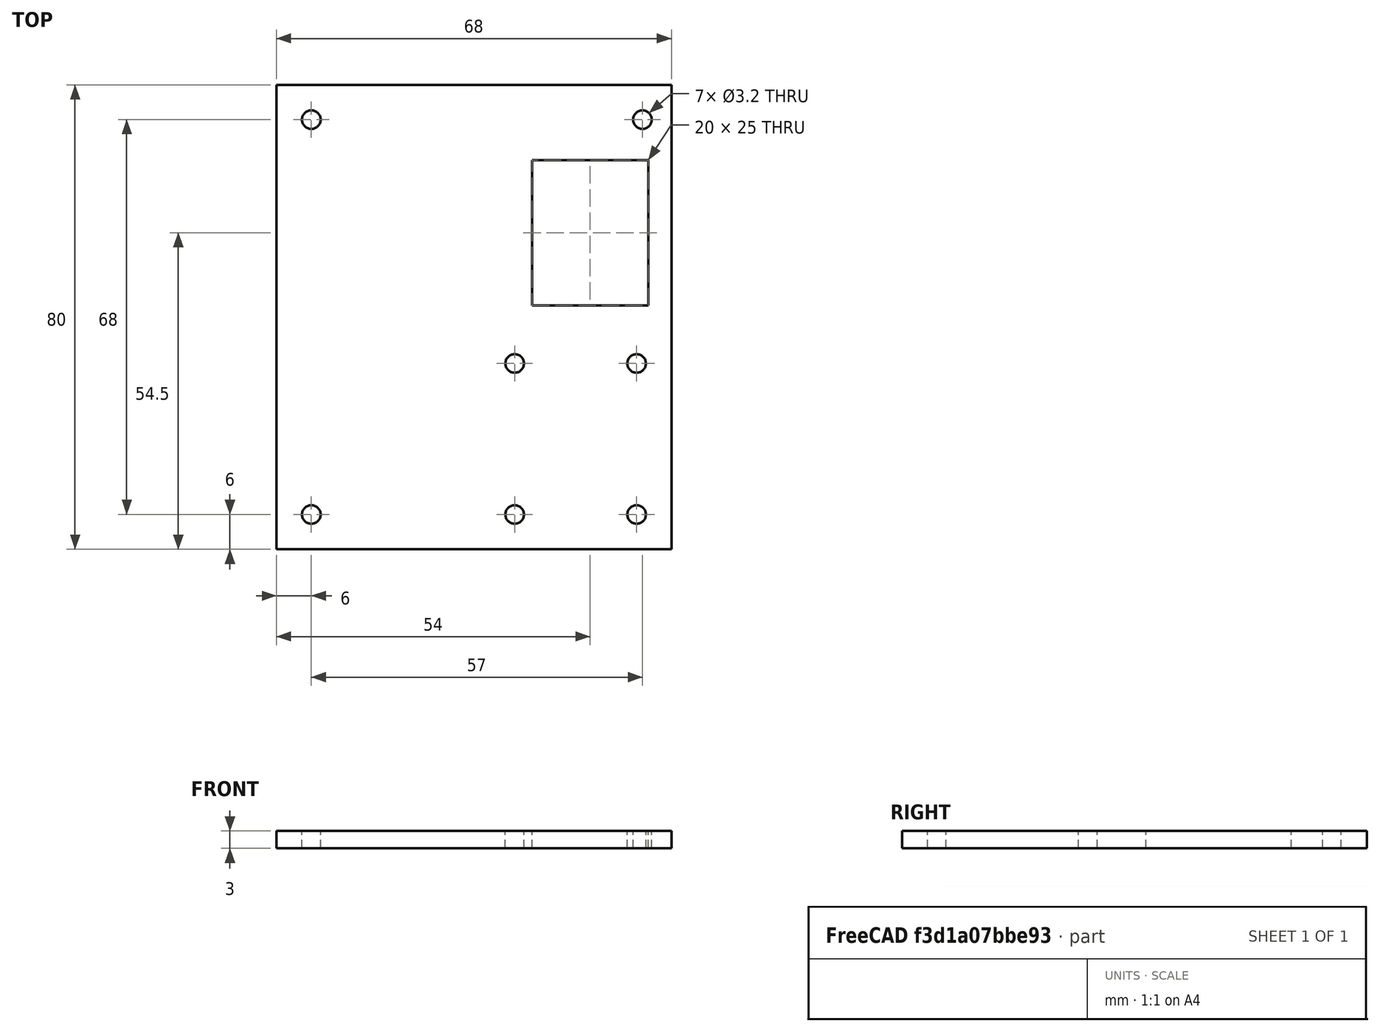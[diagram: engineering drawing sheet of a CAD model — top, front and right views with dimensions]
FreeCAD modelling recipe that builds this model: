
FCSTD DOCUMENT  (FreeCAD 0.19R24276 (Git))
Label: tapaCajaJoystick
License: All rights reserved
LicenseURL: http://en.wikipedia.org/wiki/All_rights_reserved
objects: Part::Cylinder×7, Part::Box×2, Part::Cut×2, Part::MultiFuse×1, Mesh::Feature×1
note: 12 computed .brp shape members not serialized (recipe doc carries the construction recipe); baked Part::Feature solids carry a one-line shape summary decoded from their .brp

FEATURE [Part::Box] Box020  label="Cube016"
  AttacherType = Attacher::AttachEngine3D
  Height = 3
  Length = 68
  Placement = pos=(0,22,42) rot=(0,0,1;0rad)
  Width = 80
FEATURE [Part::Cylinder] Cylinder013
  Angle = 360
  AttacherType = Attacher::AttachEngine3D
  Height = 30
  Placement = pos=(6,28,19) rot=(0,0,1;0rad)
  Radius = 1.6
FEATURE [Part::Cylinder] Cylinder014
  Angle = 360
  AttacherType = Attacher::AttachEngine3D
  Height = 30
  Placement = pos=(62,28,19) rot=(0,0,1;0rad)
  Radius = 1.6
FEATURE [Part::Cylinder] Cylinder015
  Angle = 360
  AttacherType = Attacher::AttachEngine3D
  Height = 30
  Placement = pos=(63,96,19) rot=(0,0,1;0rad)
  Radius = 1.6
FEATURE [Part::Cylinder] Cylinder016
  Angle = 360
  AttacherType = Attacher::AttachEngine3D
  Height = 30
  Placement = pos=(6,96,19) rot=(0,0,1;0rad)
  Radius = 1.6
FEATURE [Part::Cylinder] Cylinder017
  Angle = 360
  AttacherType = Attacher::AttachEngine3D
  Height = 30
  Placement = pos=(62,54,19) rot=(0,0,1;0rad)
  Radius = 1.6
FEATURE [Part::Cylinder] Cylinder018
  Angle = 360
  AttacherType = Attacher::AttachEngine3D
  Height = 30
  Placement = pos=(41,54,19) rot=(0,0,1;0rad)
  Radius = 1.6
FEATURE [Part::Cylinder] Cylinder019
  Angle = 360
  AttacherType = Attacher::AttachEngine3D
  Height = 30
  Placement = pos=(41,28,19) rot=(0,0,1;0rad)
  Radius = 1.6
FEATURE [Part::MultiFuse] Fusion
  Shapes = -> [Cylinder013,Cylinder014,Cylinder015,Cylinder016,Cylinder017,Cylinder018,Cylinder019]
FEATURE [Part::Cut] Cut
  Base = -> Box020
  Tool = -> Fusion
FEATURE [Part::Box] Box  label="Cube"
  AttacherType = Attacher::AttachEngine3D
  Height = 10
  Length = 20
  Placement = pos=(44,64,39) rot=(0,0,1;0rad)
  Width = 25
FEATURE [Part::Cut] Cut001
  Base = -> Cut
  Tool = -> Box
FEATURE [Mesh::Feature] Mesh  label="Cut001 (Meshed)"
